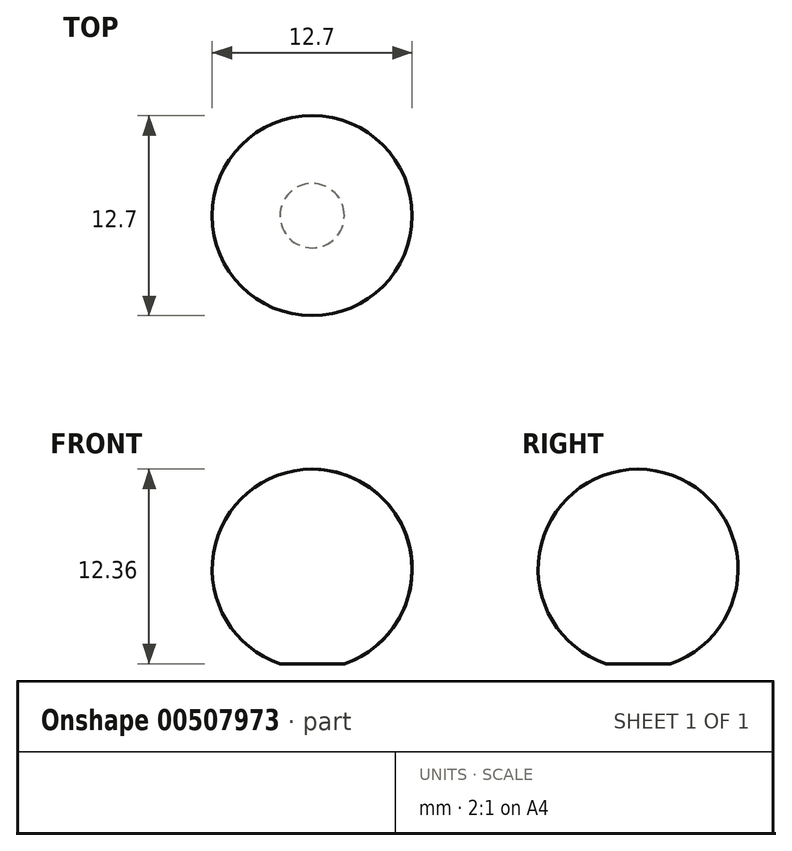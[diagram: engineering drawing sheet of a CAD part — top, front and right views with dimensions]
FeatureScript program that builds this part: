
annotation { "Feature Type Name" : "Feature", "Feature Type Description" : "" }
export const myFeature = defineFeature(function(context is Context, id is Id, definition is map)
    precondition{}
    {
        {
            var Q0;
            Q0=qCreatedBy(makeId("Front.planeOp"),FACE);
            var sketch = newSketch(context, id + "F0", { "sketchPlane" : qUnion([Q0])});
            skArc(sketch, "E0", {"start": v(0, 6.35) * mm, "mid": v(-6.26, 1.04) * mm, "end": v(-2.04, -6.01) * mm});
            skLineSegment(sketch, "E1", {"start": v(0, 6.35) * mm, "end": v(0, -6.01) * mm});
            skLineSegment(sketch, "E2", {"start": v(0, -6.01) * mm, "end": v(-2.04, -6.01) * mm});
            skSolve(sketch);
        }
        {
            var Q0;
            Q0=makeQuery(id+"F0.imprint","IMPRINT",FACE,{"disambiguationData":[TD([[makeQuery(id+"F0.imprint","IMPRINT",EDGE,{"derivedFrom":sQuery(id+"F0.wireOp",EDGE,"E0")}),1.0]])]});
            var Q1;
            Q1=sQuery(id+"F0.wireOp",EDGE,"E1");
            revolve(context, id + "F1", {"entities" : qUnion([Q0]), "axis" : qUnion([Q1]), "revolveType" : RevolveType.FULL});
        }
    });
